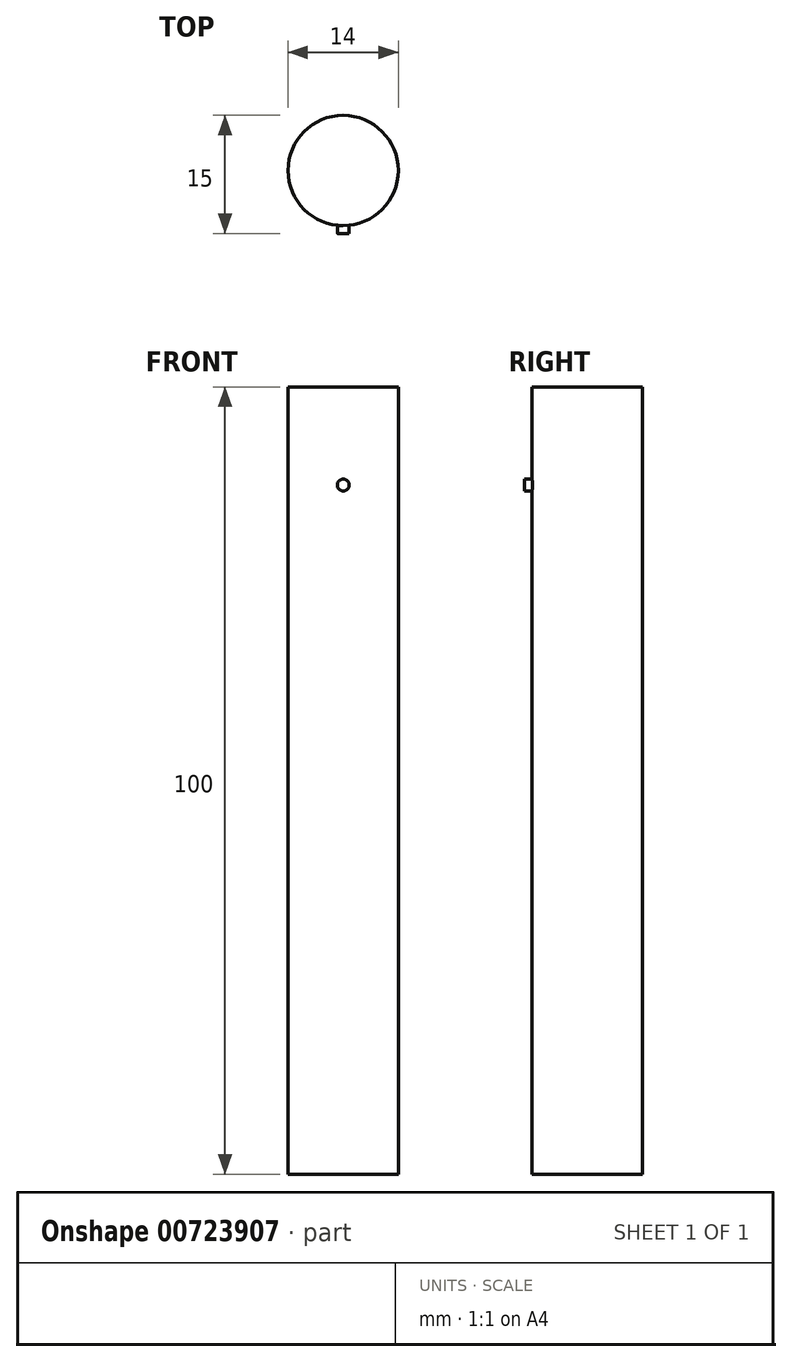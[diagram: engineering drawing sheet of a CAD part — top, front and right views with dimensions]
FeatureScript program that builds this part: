
annotation { "Feature Type Name" : "Feature", "Feature Type Description" : "" }
export const myFeature = defineFeature(function(context is Context, id is Id, definition is map)
    precondition{}
    {
        {
            var Q0;
            Q0=qCreatedBy(makeId("Top.planeOp"),FACE);
            var sketch = newSketch(context, id + "F0", { "sketchPlane" : qUnion([Q0])});
            skCircle(sketch, "E0", {"center": v(0, 0) * mm, "radius": 7 * mm});
            skSolve(sketch);
        }
        {
            var Q0;
            Q0 = qSketchRegion(id + "F0", true);
            extrude(context, id + "F1", {"entities" : qUnion([Q0]), "depth" : 100 * mm, "offsetDistance" : 25 * mm});
        }
        {
            var Q0;
            Q0=qCreatedBy(makeId("Front.planeOp"),FACE);
            var sketch = newSketch(context, id + "F2", { "sketchPlane" : qUnion([Q0])});
            skLineSegment(sketch, "E1", {"start": v(0, -4.46) * mm, "end": v(0, 109.64) * mm, "construction": true});
            skCircle(sketch, "E2", {"center": v(0, 87.54) * mm, "radius": 0.75 * mm});
            skSolve(sketch);
        }
        {
            var Q0;
            Q0 = qSketchRegion(id + "F2", true);
            extrude(context, id + "F3", {"entities" : qUnion([Q0]), "operationType" : NewBodyOperationType.ADD, "depth" : 8 * mm, "offsetDistance" : 25 * mm});
        }
    });
